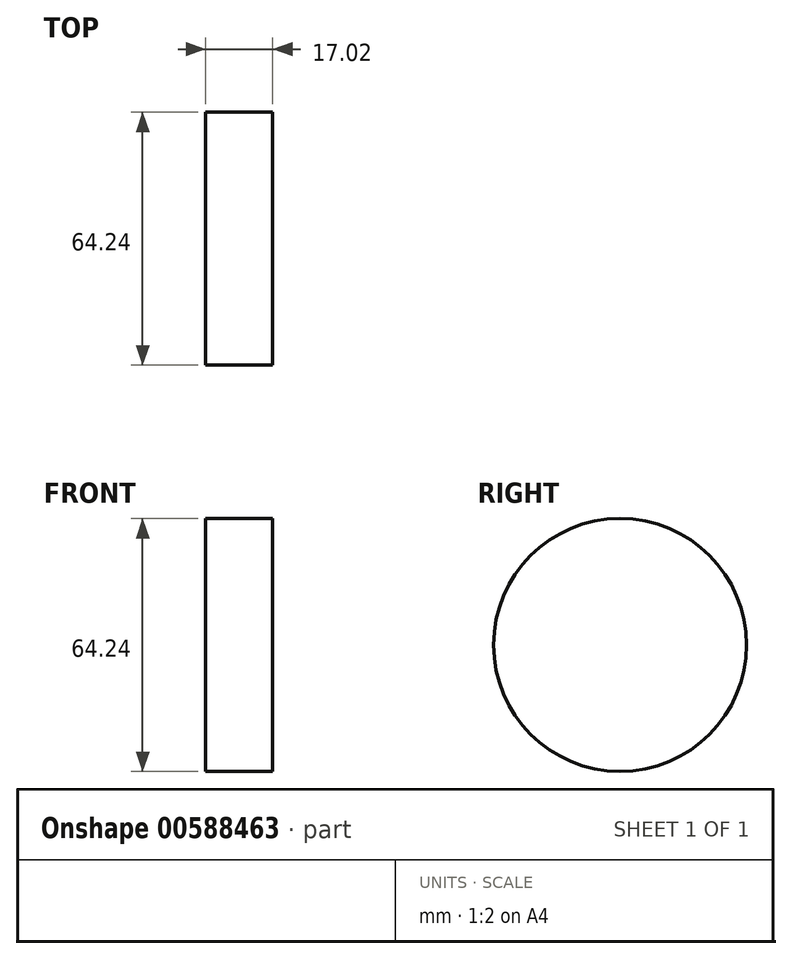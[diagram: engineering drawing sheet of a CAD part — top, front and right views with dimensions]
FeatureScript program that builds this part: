
annotation { "Feature Type Name" : "Feature", "Feature Type Description" : "" }
export const myFeature = defineFeature(function(context is Context, id is Id, definition is map)
    precondition{}
    {
        {
            var Q0;
            Q0=qCreatedBy(makeId("Right.planeOp"),FACE);
            var sketch = newSketch(context, id + "F0", { "sketchPlane" : qUnion([Q0])});
            skCircle(sketch, "E0", {"center": v(0, 0) * mm, "radius": 32.12 * mm});
            skSolve(sketch);
        }
        {
            var Q0;
            Q0=makeQuery(id+"F0.imprint","IMPRINT",FACE,{"disambiguationData":[TD([[makeQuery(id+"F0.imprint","IMPRINT",EDGE,{"derivedFrom":sQuery(id+"F0.wireOp",EDGE,"E0")}),1.0]])]});
            extrude(context, id + "F1", {"entities" : qUnion([Q0]), "depth" : 17.02 * mm, "offsetDistance" : 25.4 * mm});
        }
    });
